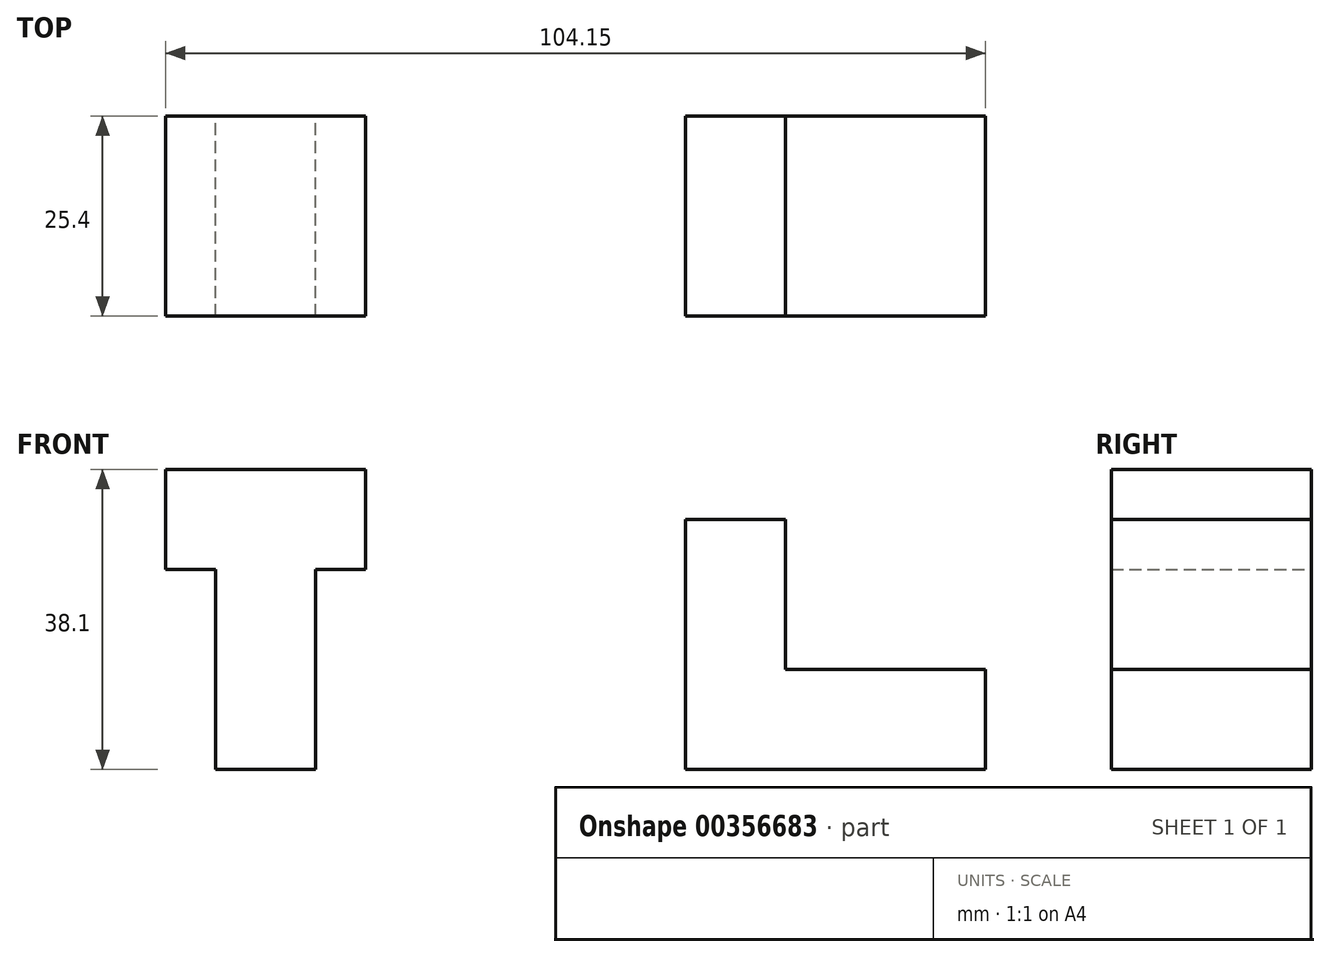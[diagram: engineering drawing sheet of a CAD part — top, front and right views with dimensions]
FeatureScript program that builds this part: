
annotation { "Feature Type Name" : "Feature", "Feature Type Description" : "" }
export const myFeature = defineFeature(function(context is Context, id is Id, definition is map)
    precondition{}
    {
        {
            var Q0;
            Q0=qCreatedBy(makeId("Front.planeOp"),FACE);
            var sketch = newSketch(context, id + "F0", { "sketchPlane" : qUnion([Q0])});
            skLineSegment(sketch, "E0", {"start": v(35.9, 0) * mm, "end": v(35.9, 31.75) * mm});
            skLineSegment(sketch, "E1", {"start": v(35.9, 31.75) * mm, "end": v(48.6, 31.75) * mm});
            skLineSegment(sketch, "E2", {"start": v(48.6, 31.75) * mm, "end": v(48.6, 12.7) * mm});
            skLineSegment(sketch, "E3", {"start": v(48.6, 12.7) * mm, "end": v(74, 12.7) * mm});
            skLineSegment(sketch, "E4", {"start": v(74, 12.7) * mm, "end": v(74, 0) * mm});
            skLineSegment(sketch, "E5", {"start": v(74, 0) * mm, "end": v(35.9, 0) * mm});
            skSolve(sketch);
        }
        {
            var Q0;
            Q0 = qSketchRegion(id + "F0", true);
            extrude(context, id + "F1", {"entities" : qUnion([Q0]), "depth" : 25.4 * mm});
        }
        {
            var Q0;
            Q0=qCreatedBy(makeId("Front.planeOp"),FACE);
            var sketch = newSketch(context, id + "F2", { "sketchPlane" : qUnion([Q0])});
            skLineSegment(sketch, "E6", {"start": v(-23.8, 0) * mm, "end": v(-23.8, 25.4) * mm});
            skLineSegment(sketch, "E7", {"start": v(-23.8, 25.4) * mm, "end": v(-30.14, 25.4) * mm});
            skLineSegment(sketch, "E8", {"start": v(-30.14, 25.4) * mm, "end": v(-30.14, 38.1) * mm});
            skLineSegment(sketch, "E9", {"start": v(-30.14, 38.1) * mm, "end": v(-4.74, 38.1) * mm});
            skLineSegment(sketch, "E10", {"start": v(-4.74, 38.1) * mm, "end": v(-4.74, 25.4) * mm});
            skLineSegment(sketch, "E11", {"start": v(-4.74, 25.4) * mm, "end": v(-11.1, 25.4) * mm});
            skLineSegment(sketch, "E12", {"start": v(-11.1, 25.4) * mm, "end": v(-11.1, 0) * mm});
            skLineSegment(sketch, "E13", {"start": v(-11.1, 0) * mm, "end": v(-23.8, 0) * mm});
            skSolve(sketch);
        }
        {
            var Q0;
            Q0 = qSketchRegion(id + "F2", true);
            extrude(context, id + "F3", {"entities" : qUnion([Q0]), "depth" : 25.4 * mm});
        }
    });
